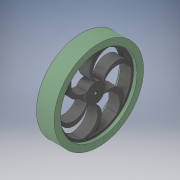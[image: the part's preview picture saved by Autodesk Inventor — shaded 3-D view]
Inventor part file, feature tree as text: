
AUTODESK INVENTOR PART (.ipt)
format: ipt  version: 2018 (Build 220112000, 112)  size: 252,928 bytes
history: native  units: in
note: dims shown in document units (in); Inventor stores cm internally (conversion verified against a paired STEP export)
features: extrude x5, sketch x5
ambient origin geometry x8: Origin, YZ Plane, XZ Plane, XY Plane, X Axis, Y Axis, Z Axis, Center Point
bodies: Solid1 (feature_tree), Solid3 (feature_tree)
feature tree (10):
  extrude  "Extrusion1"  Depth=0.3937in
  extrude  "Extrusion2"  Depth=0.1969in
  extrude  "Extrusion3"  Depth=0.7874in TaperAngle=360.0deg
  extrude  "Extrusion4"  Depth=0.7874in
  extrude  "Extrusion5"  Depth=0.5in
  sketch  "Sketch1"  dims[d0=4.0in d1=0.3937in]
  sketch  "Sketch2"  dims[d2=1.1811in d3=0.1969in]
  sketch  "Sketch3"  dims[d4=0.7874in d5=0.0in d6=2.3622in d8=360.0deg]
  sketch  "Sketch4"  dims[d10=0.7874in d11=0.0in d12=3.4173in]
  sketch  "Sketch5"  dims[d13=0.15in d14=0.0in d15=3.417in d16=0.15in d17=0.0in d18=0.118in d19=0.118in d20=0.045in d21=0.5in d22=0.0in]
